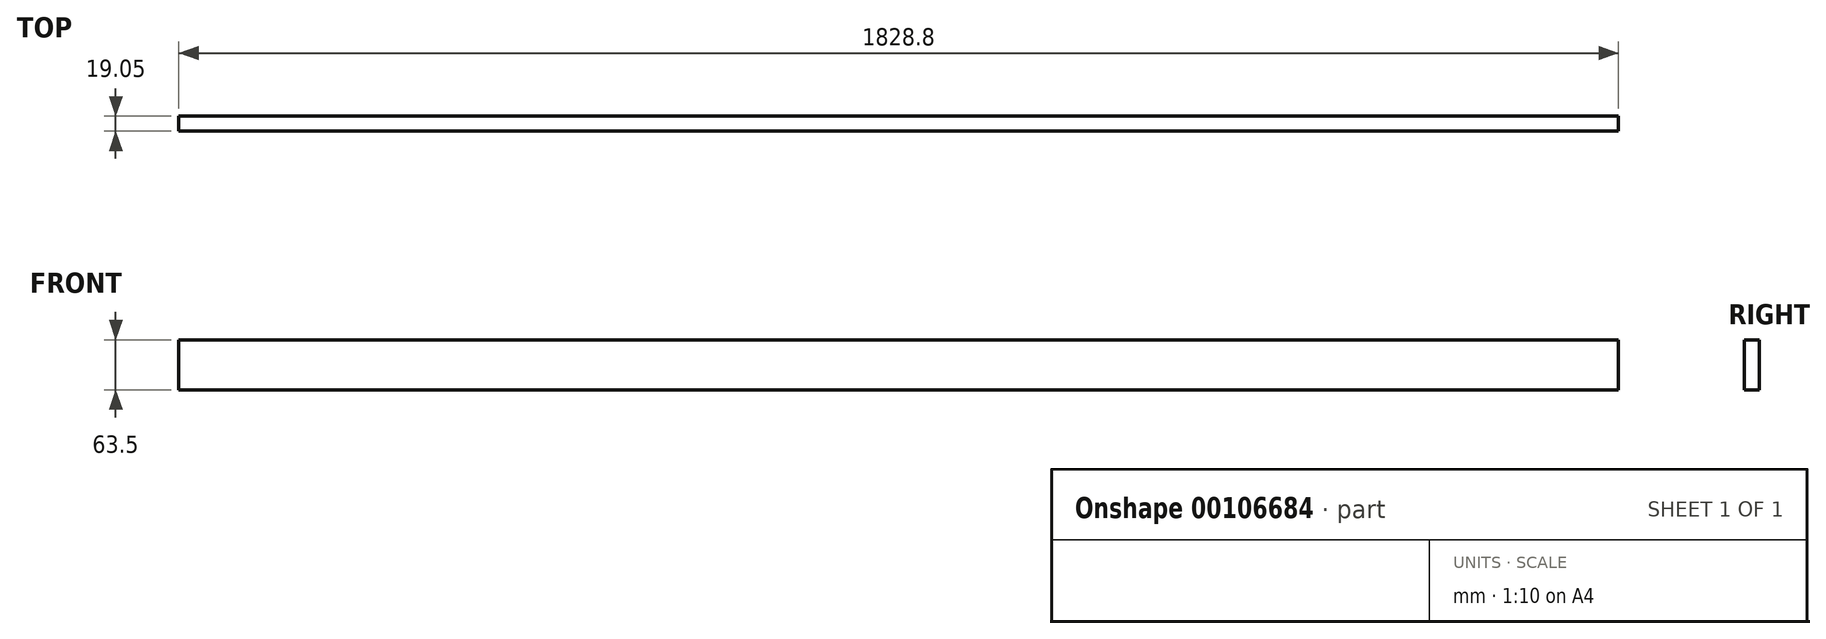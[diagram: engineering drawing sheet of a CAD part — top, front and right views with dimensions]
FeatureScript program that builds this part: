
annotation { "Feature Type Name" : "Feature", "Feature Type Description" : "" }
export const myFeature = defineFeature(function(context is Context, id is Id, definition is map)
    precondition{}
    {
        {
            var Q0;
            Q0=qCreatedBy(makeId("Front.planeOp"),FACE);
            var sketch = newSketch(context, id + "F0", { "sketchPlane" : qUnion([Q0])});
            skLineSegment(sketch, "E0.bottom", {"start": v(0, 0) * mm, "end": v(1828.8, 0) * mm});
            skLineSegment(sketch, "E0.top", {"start": v(0, 63.5) * mm, "end": v(1828.8, 63.5) * mm});
            skLineSegment(sketch, "E0.left", {"start": v(0, 0) * mm, "end": v(0, 63.5) * mm});
            skLineSegment(sketch, "E0.right", {"start": v(1828.8, 0) * mm, "end": v(1828.8, 63.5) * mm});
            skSolve(sketch);
        }
        {
            var Q0;
            Q0=makeQuery(id+"F0.imprint","IMPRINT",FACE,{"disambiguationData":[TD([[makeQuery(id+"F0.imprint","IMPRINT",EDGE,{"derivedFrom":sQuery(id+"F0.wireOp",EDGE,"E0.bottom")}),1.0]])]});
            extrude(context, id + "F1", {"entities" : qUnion([Q0]), "depth" : 19.05 * mm});
        }
    });
